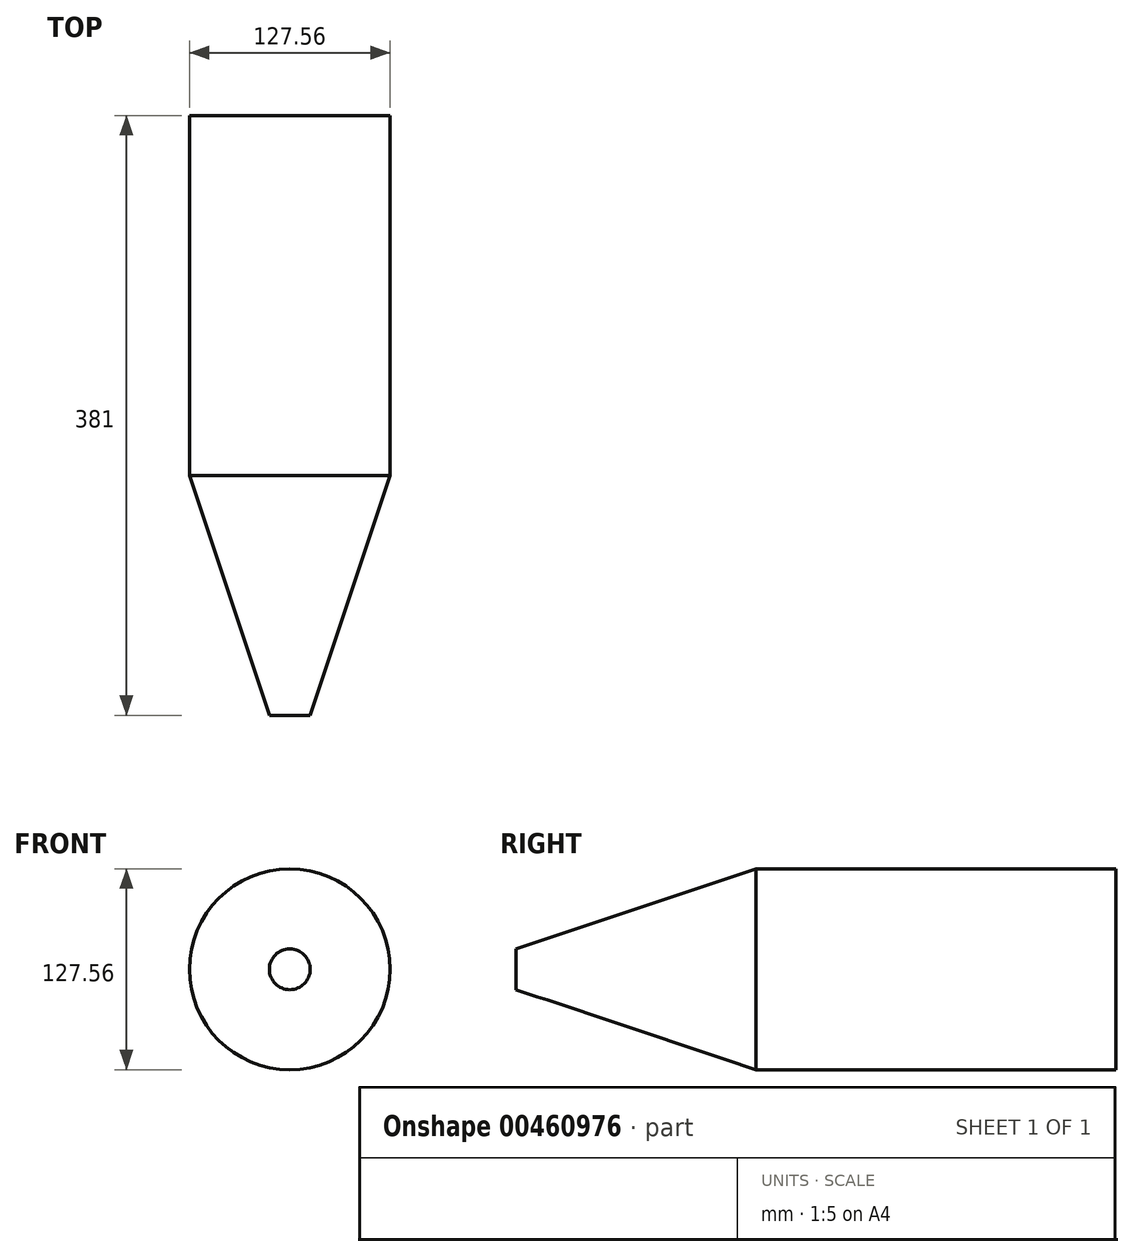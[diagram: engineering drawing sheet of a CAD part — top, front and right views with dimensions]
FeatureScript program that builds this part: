
annotation { "Feature Type Name" : "Feature", "Feature Type Description" : "" }
export const myFeature = defineFeature(function(context is Context, id is Id, definition is map)
    precondition{}
    {
        {
            var Q0;
            Q0=qCreatedBy(makeId("Front.planeOp"),FACE);
            var sketch = newSketch(context, id + "F0", { "sketchPlane" : qUnion([Q0])});
            skCircle(sketch, "E0", {"center": v(0, 0) * mm, "radius": 63.78 * mm});
            skSolve(sketch);
        }
        {
            var Q0;
            Q0 = qSketchRegion(id + "F0", true);
            extrude(context, id + "F1", {"entities" : qUnion([Q0]), "depth" : 381 * mm});
        }
        {
            var Q0;
            Q0=qCreatedBy(makeId("Right.planeOp"),FACE);
            var sketch = newSketch(context, id + "F2", { "sketchPlane" : qUnion([Q0])});
            skLineSegment(sketch, "E1", {"start": v(0, 0) * mm, "end": v(-460.9, 0) * mm, "construction": true});
            skLineSegment(sketch, "E2", {"start": v(-381, 12.98) * mm, "end": v(-228.6, 63.78) * mm});
            skLineSegment(sketch, "E3", {"start": v(-228.6, 63.78) * mm, "end": v(-381, 63.78) * mm});
            skLineSegment(sketch, "E4", {"start": v(-381, 63.78) * mm, "end": v(-381, 12.98) * mm});
            skSolve(sketch);
        }
        {
            var Q0;
            Q0 = qSketchRegion(id + "F2", true);
            var Q1;
            Q1=sQuery(id+"F2.wireOp",EDGE,"E1");
            revolve(context, id + "F3", {"operationType" : NewBodyOperationType.REMOVE, "entities" : qUnion([Q0]), "axis" : qUnion([Q1]), "revolveType" : RevolveType.FULL, "oppositeDirection" : true});
        }
        {
            var Q0;
            Q0=makeQuery(id+"F1.opExtrude","CAP_FACE",FACE,{"disambiguationData":[OSD([sQuery(id+"F0.wireOp",EDGE,"E0")])],"isStart":false});
            var sketch = newSketch(context, id + "F4", { "sketchPlane" : qUnion([Q0])});
            skLineSegment(sketch, "E5", {"start": v(2.54, 12.99) * mm, "end": v(2.54, 2.54) * mm});
            skLineSegment(sketch, "E6", {"start": v(2.54, 2.54) * mm, "end": v(12.99, 2.54) * mm});
            skArc(sketch, "E7", {"start": v(2.54, 12.99) * mm, "mid": v(9.36, 9.36) * mm, "end": v(12.99, 2.54) * mm});
            skSolve(sketch);
        }
        {
            var Q0;
            {var subQ0=sQuery(id+"F4.wireOp",EDGE,"E6");var subQ1=sQuery(id+"F4.wireOp",EDGE,"E5");var subQ2=makeQuery(id+"F4.imprint","INTERSECT",VERTEX,{"derivedFrom":[subQ1,subQ0]});Q0=makeQuery(id+"F4.imprint","IMPRINT",FACE,{"disambiguationData":[TD([[makeQuery(id+"F4.imprint","IMPRINT",EDGE,{"disambiguationData":[TD([[subQ2,1.0]])],"derivedFrom":subQ1}),-1.0]])]});}
            cPlane(context, id + "F5", {"entities" : qUnion([Q0]), "cplaneType" : CPlaneType.OFFSET, "offset" : 152.4 * mm, "oppositeDirection" : true, "width" : 152.4 * mm, "height" : 152.4 * mm});
        }
    });
